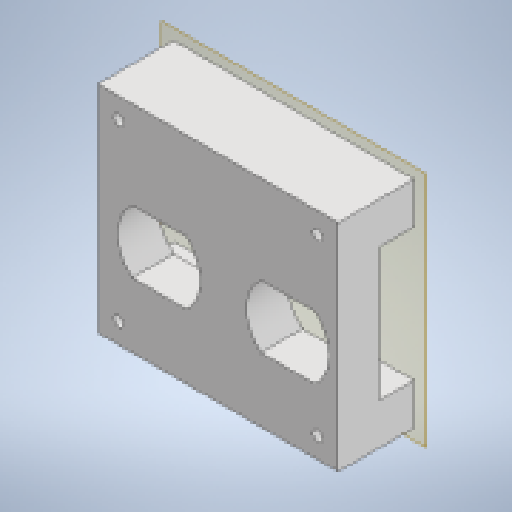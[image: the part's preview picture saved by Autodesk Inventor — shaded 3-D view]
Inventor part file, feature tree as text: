
AUTODESK INVENTOR PART (.ipt)
format: ipt  version: 2023 (Build 270158000, 158)  size: 259,072 bytes
history: native  units: mm
features: other x7, reference x5, extrude x3, sketch x3, plane x2, projected_geometry x1
ambient origin geometry x8: Origin, YZ Plane, XZ Plane, XY Plane, X Axis, Y Axis, Z Axis, Center Point
bodies: Solid1 (feature_tree)
feature tree (21):
  plane  "Work Plane1"
  extrude  "Extrusion1"  Depth=0.1mm
  extrude  "Extrusion2"  Depth=10.0mm
  plane  "Work Plane2"
  extrude  "Extrusion3"  Depth=8.3mm TaperAngle=0.0deg
  sketch  "Sketch1"  dims[d0=0.1mm d1=0.1mm]
  reference  "Reference1"
  reference  "Reference2"
  reference  "Reference3"
  reference  "Reference4"
  sketch  "Sketch2"  dims[d2=10.0mm d3=10.0mm]
  sketch  "Sketch3"  dims[d4=20.0mm d6=42.149mm d7=20.0mm d9=48.171mm d12=8.3mm d13=0.0mm d14=10.0mm d15=0.0mm d16=-3.5mm d17=0.5mm d18=20.0mm d20=42.149mm d21=20.0mm d23=48.171mm d26=30.75mm d27=0.0mm]
  reference  "Reference5"
  projected_geometry  "Projected Loop1"
  parser-record x1  (decoder bookkeeping rows leaked as tree rows — omitted from the tree; the rows remain in map.json)
  other  "doorLockAssembly_V5.iam"
  other  "housePlate_V5:1"
  other  "motor:2"
  other  "motor:1"
  other  "rack_V3:1"
  other  "screw:1"
note: 1 file-system path scrubbed to <path> (originals preserved in map.json)
